# Revit family: TYCO-FPP-Zettler-QIO850 Quad inputoutput module
name_source: partatom
category: Electrical Fixtures
revit_build: Autodesk Revit 2014 (Build: 20130308_1515(x64)
units: mm (PartAtom-declared; Revit-internal decimal feet)

## types (1)
- TYCO-FPP-Zettler-QIO850 Quad inputoutput module
    Alarm current = 3.6 mA
    Approvals = EN54-17, EN54-18 and
EN54-13
    Aux. Voltage Input = 20-55Vdc
    Description = The MX Quad Ancillary Modules form a versatile new
range of multiple input and output modules for use
with MX TECHNOLOGY systems1.
    Input EOL = 3k3 Ohm
    Keynote = Two-way IR communication with
850EMT saves commissioning time
    Length = 103 mm
    Manufacturer = Tyco
    Model = Zettler -555.800.071
    Operating Humidity = Up to 95 %
    Operating Temperature = -25 to +70 oC
    PCB = PCB
    Quiescent Current = 0.58mA
    RS = RS
    RSS = res
    Relay Output = 2A@30Vdc
    ST = ST12
    Storage Temparature = 40 to +80 oC
    Type Comments = QIO850 - Quad Input / Output module – provides four
monitored inputs and four relay outputs
    URL = https://www.tycosafetyproducts-anz.com
    Width = 134 mm

## geometry (parser evidence)
native form markers: Sweep x1
no freeform markers — native parametric forms only
